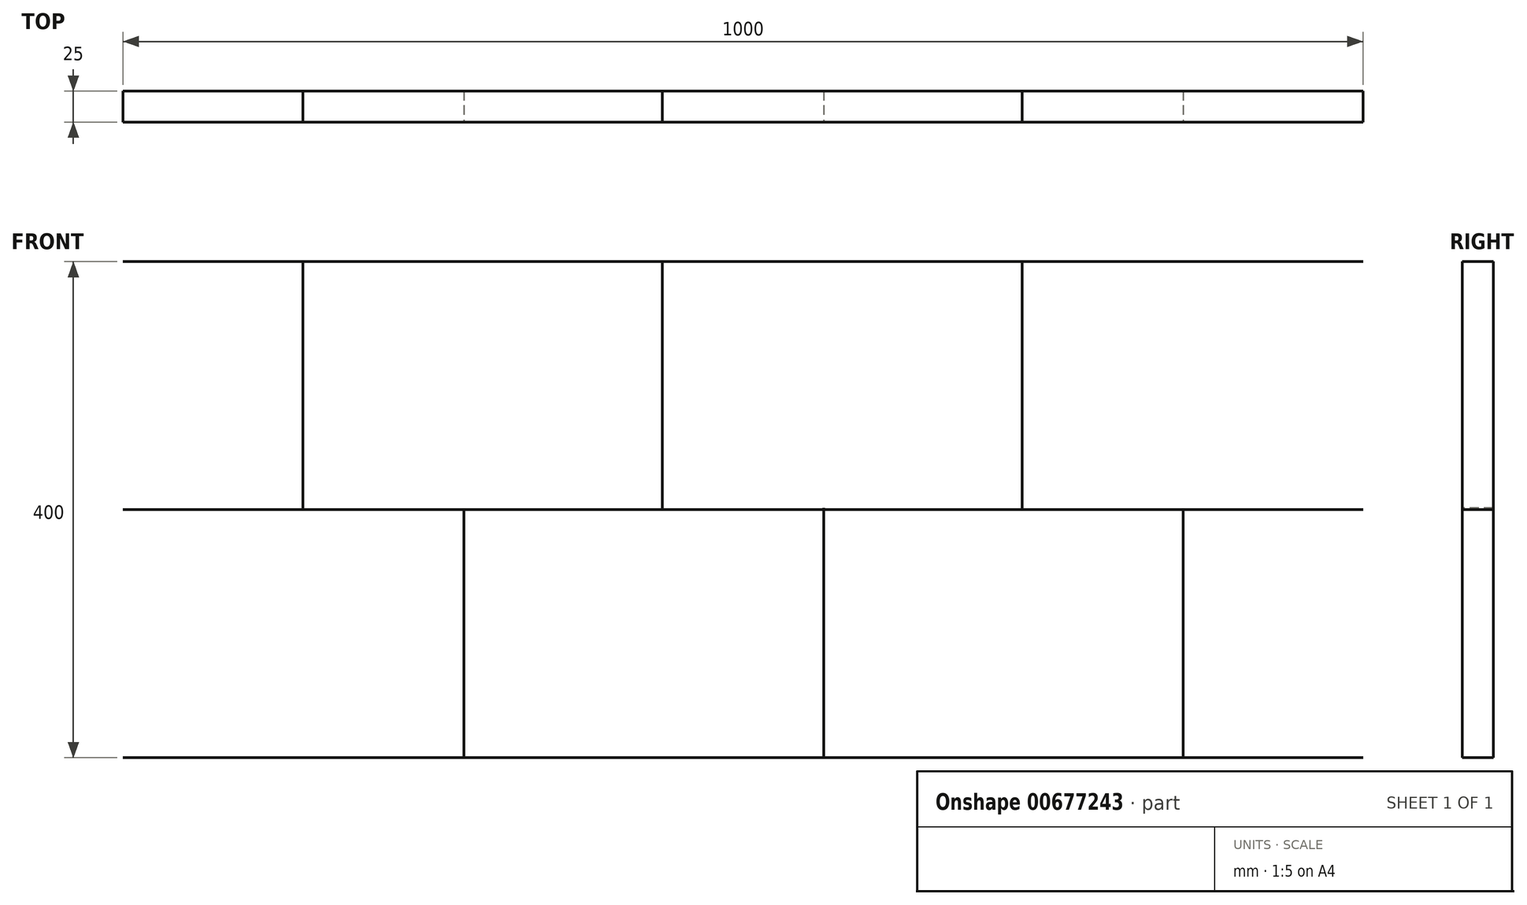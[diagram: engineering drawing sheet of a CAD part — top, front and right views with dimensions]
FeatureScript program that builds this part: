
annotation { "Feature Type Name" : "Feature", "Feature Type Description" : "" }
export const myFeature = defineFeature(function(context is Context, id is Id, definition is map)
    precondition{}
    {
        {
            var Q0;
            Q0=qCreatedBy(makeId("Front.planeOp"),FACE);
            var sketch = newSketch(context, id + "F0", { "sketchPlane" : qUnion([Q0])});
            skLineSegment(sketch, "E0.bottom", {"start": v(-505.38, 71.6) * mm, "end": v(494.62, 71.6) * mm});
            skLineSegment(sketch, "E0.top", {"start": v(-505.38, -128.4) * mm, "end": v(494.62, -128.4) * mm});
            skLineSegment(sketch, "E0.left", {"start": v(-505.38, 71.6) * mm, "end": v(-505.38, -128.4) * mm});
            skLineSegment(sketch, "E0.right", {"start": v(494.62, 71.6) * mm, "end": v(494.62, -128.4) * mm});
            skLineSegment(sketch, "E1", {"start": v(-505.38, -128.4) * mm, "end": v(-505.38, -328.4) * mm});
            skLineSegment(sketch, "E2", {"start": v(-505.38, -328.4) * mm, "end": v(494.62, -328.4) * mm});
            skLineSegment(sketch, "E3", {"start": v(494.62, -328.4) * mm, "end": v(494.62, -128.4) * mm});
            skLineSegment(sketch, "E4", {"start": v(-360.38, 71.6) * mm, "end": v(-360.38, -128.4) * mm});
            skLineSegment(sketch, "E5", {"start": v(-70.38, 71.6) * mm, "end": v(-70.38, -128.4) * mm});
            skLineSegment(sketch, "E6", {"start": v(219.62, 71.6) * mm, "end": v(219.62, -128.4) * mm});
            skLineSegment(sketch, "E7", {"start": v(349.62, -128.4) * mm, "end": v(349.62, -328.4) * mm});
            skLineSegment(sketch, "E8", {"start": v(59.62, -127.04) * mm, "end": v(59.62, -328.4) * mm});
            skLineSegment(sketch, "E9", {"start": v(-230.38, -128.4) * mm, "end": v(-230.38, -328.4) * mm});
            skSolve(sketch);
        }
        {
            var Q0;
            Q0=sQuery(id+"F0.wireOp",EDGE,"E2");
            var Q1;
            Q1=sQuery(id+"F0.wireOp",EDGE,"E0.bottom");
            var Q2;
            Q2=sQuery(id+"F0.wireOp",EDGE,"E0.top");
            extrude(context, id + "F1", {"bodyType" : ToolBodyType.SURFACE, "surfaceEntities" : qUnion([Q0, Q1, Q2]), "depth" : 25 * mm, "offsetDistance" : 25 * mm});
        }
        {
            var Q0;
            Q0=sQuery(id+"F0.wireOp",EDGE,"E4");
            var Q1;
            Q1=sQuery(id+"F0.wireOp",EDGE,"E5");
            var Q2;
            Q2=sQuery(id+"F0.wireOp",EDGE,"E9");
            var Q3;
            Q3=sQuery(id+"F0.wireOp",EDGE,"E8");
            var Q4;
            Q4=sQuery(id+"F0.wireOp",EDGE,"E6");
            var Q5;
            Q5=sQuery(id+"F0.wireOp",EDGE,"E7");
            extrude(context, id + "F2", {"bodyType" : ToolBodyType.SURFACE, "surfaceEntities" : qUnion([Q0, Q1, Q2, Q3, Q4, Q5]), "depth" : 25 * mm, "offsetDistance" : 25 * mm});
        }
    });
